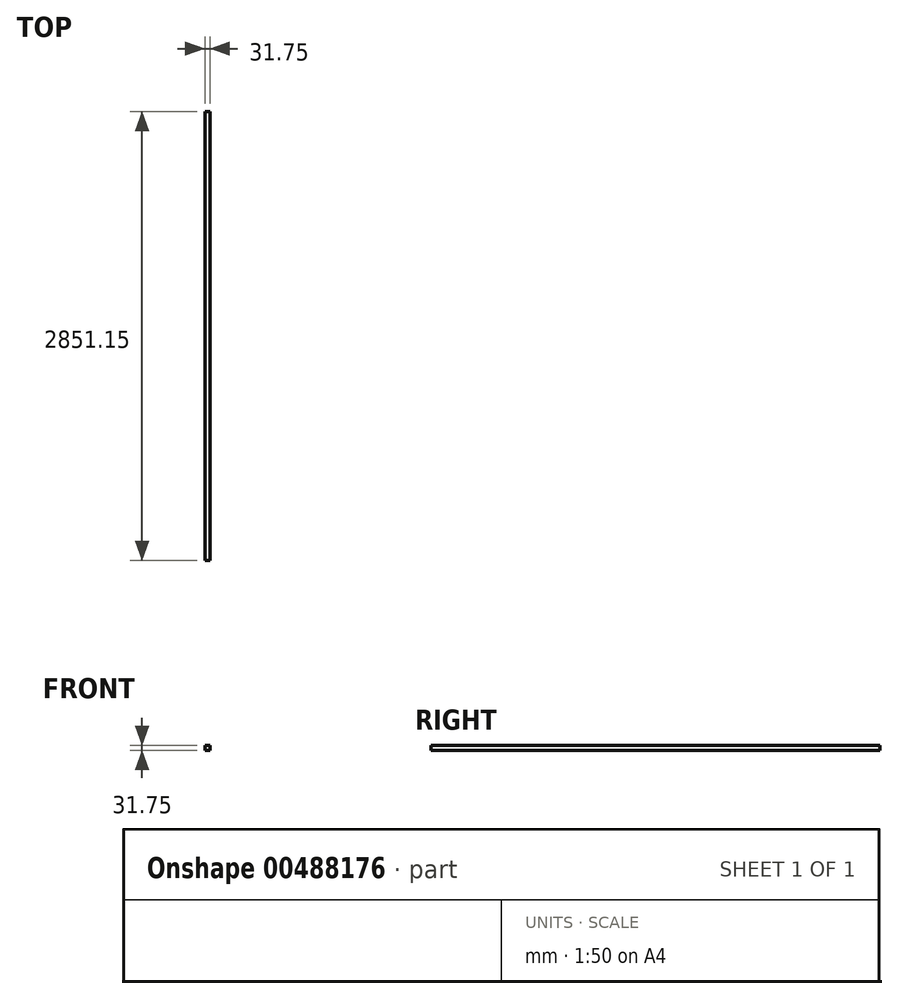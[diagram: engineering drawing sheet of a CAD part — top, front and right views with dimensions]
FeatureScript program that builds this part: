
annotation { "Feature Type Name" : "Feature", "Feature Type Description" : "" }
export const myFeature = defineFeature(function(context is Context, id is Id, definition is map)
    precondition{}
    {
        {
            var Q0;
            Q0=qCreatedBy(makeId("Front.planeOp"),FACE);
            var sketch = newSketch(context, id + "F0", { "sketchPlane" : qUnion([Q0])});
            skLineSegment(sketch, "E0", {"start": v(0, 0) * mm, "end": v(0, 31.75) * mm});
            skLineSegment(sketch, "E1", {"start": v(0, 31.75) * mm, "end": v(31.75, 31.75) * mm});
            skLineSegment(sketch, "E2", {"start": v(31.75, 31.75) * mm, "end": v(31.75, 0) * mm});
            skLineSegment(sketch, "E3", {"start": v(31.75, 0) * mm, "end": v(0, 0) * mm});
            skSolve(sketch);
        }
        {
            var Q0;
            Q0=makeQuery(id+"F0.imprint","IMPRINT",FACE,{"disambiguationData":[TD([[makeQuery(id+"F0.imprint","IMPRINT",EDGE,{"derivedFrom":sQuery(id+"F0.wireOp",EDGE,"E0")}),-1.0]])]});
            extrude(context, id + "F1", {"entities" : qUnion([Q0]), "oppositeDirection" : true, "depth" : 2851.15 * mm, "offsetDistance" : 25.4 * mm});
        }
    });
